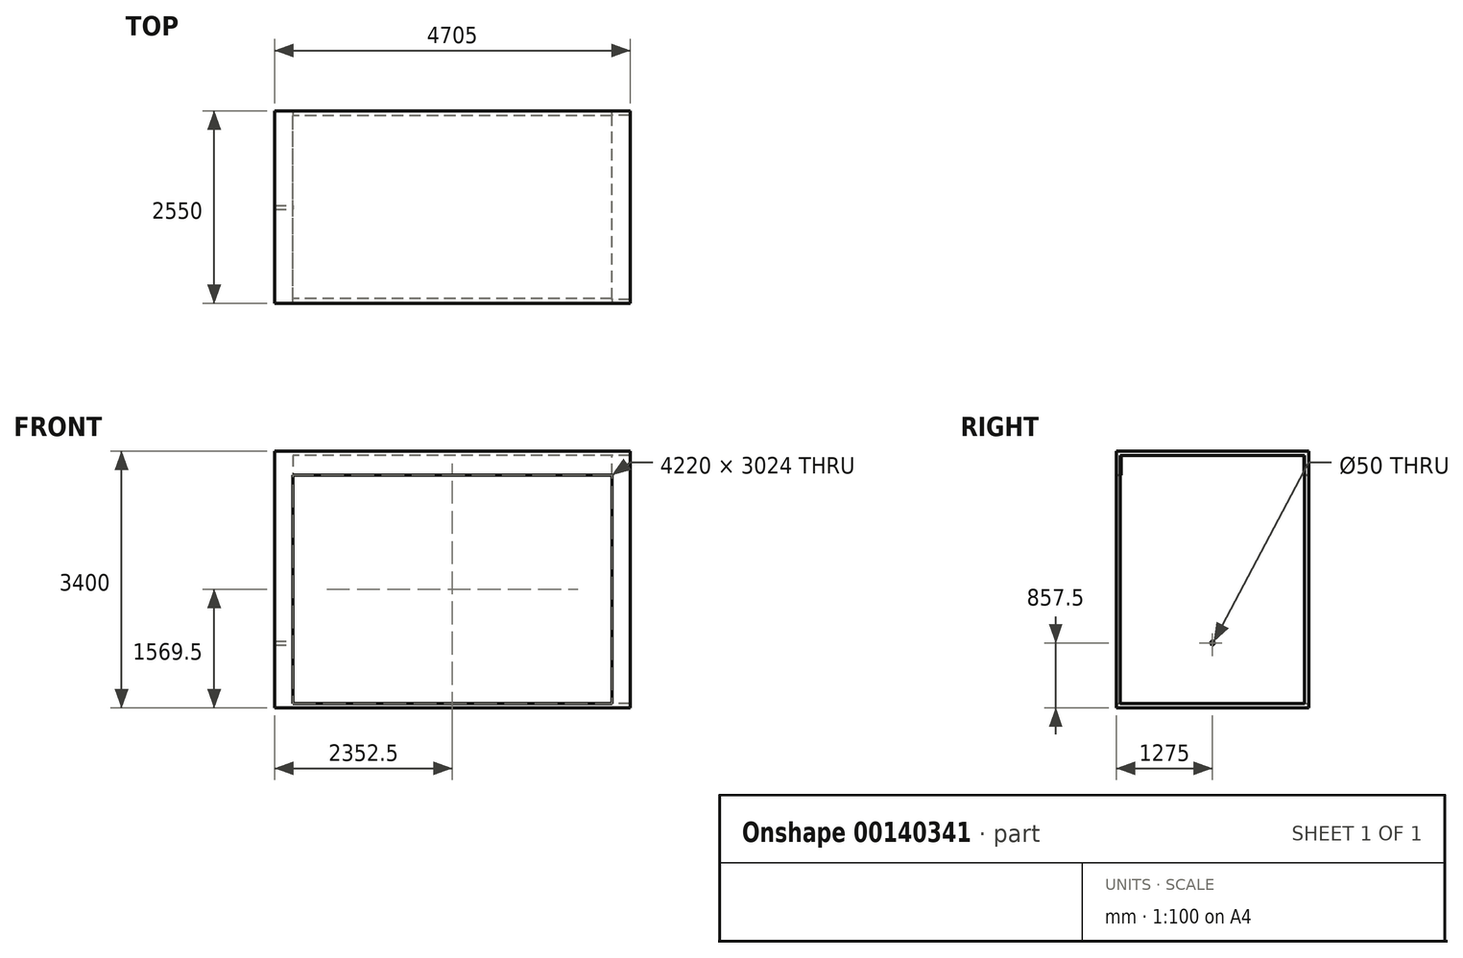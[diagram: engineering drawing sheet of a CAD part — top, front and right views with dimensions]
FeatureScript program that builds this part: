
annotation { "Feature Type Name" : "Feature", "Feature Type Description" : "" }
export const myFeature = defineFeature(function(context is Context, id is Id, definition is map)
    precondition{}
    {
        {
            var Q0;
            Q0=qCreatedBy(makeId("Front.planeOp"),FACE);
            var sketch = newSketch(context, id + "F0", { "sketchPlane" : qUnion([Q0])});
            skLineSegment(sketch, "E0.bottom", {"start": v(2352.5, -1700) * mm, "end": v(-2352.5, -1700) * mm});
            skLineSegment(sketch, "E0.top", {"start": v(2352.5, 1700) * mm, "end": v(-2352.5, 1700) * mm});
            skLineSegment(sketch, "E0.left", {"start": v(2352.5, -1700) * mm, "end": v(2352.5, 1700) * mm});
            skLineSegment(sketch, "E0.right", {"start": v(-2352.5, -1700) * mm, "end": v(-2352.5, 1700) * mm});
            skPoint(sketch, "E0.middle", {"position": v(0, 0) * mm});
            skLineSegment(sketch, "E1.bottom", {"start": v(2110, -1642.5) * mm, "end": v(-2110, -1642.5) * mm});
            skLineSegment(sketch, "E1.top", {"start": v(2110, 1642.5) * mm, "end": v(-2110, 1642.5) * mm});
            skLineSegment(sketch, "E1.left", {"start": v(2110, -1642.5) * mm, "end": v(2110, 1642.5) * mm});
            skLineSegment(sketch, "E1.right", {"start": v(-2110, -1642.5) * mm, "end": v(-2110, 1642.5) * mm});
            skSolve(sketch);
        }
        {
            var Q0;
            Q0=qSketchRegion(id+"F0",true);
            extrude(context, id + "F1", {"entities" : qUnion([Q0]), "depth" : 2550 * mm});
        }
        {
            var Q0;
            Q0=makeQuery(id+"F1.opExtrude","SWEPT_FACE",FACE,{"disambiguationData":[OSD([sQuery(id+"F0.wireOp",EDGE,"E1.right")])]});
            var sketch = newSketch(context, id + "F2", { "sketchPlane" : qUnion([Q0])});
            skLineSegment(sketch, "E2.bottom", {"start": v(-2550, 1642.5) * mm, "end": v(-2485, 1642.5) * mm});
            skLineSegment(sketch, "E2.top", {"start": v(-2550, 1381.5) * mm, "end": v(-2485, 1381.5) * mm});
            skLineSegment(sketch, "E2.left", {"start": v(-2550, 1642.5) * mm, "end": v(-2550, 1381.5) * mm});
            skLineSegment(sketch, "E2.right", {"start": v(-2485, 1642.5) * mm, "end": v(-2485, 1381.5) * mm});
            skLineSegment(sketch, "E3", {"start": v(-1275, -1642.5) * mm, "end": v(-1275, 507.53) * mm, "construction": true});
            skLineSegment(sketch, "E4.MirrorCS", {"start": v(0, 1642.5) * mm, "end": v(0, 1381.5) * mm});
            skLineSegment(sketch, "E5.MirrorCS", {"start": v(-65, 1642.5) * mm, "end": v(-65, 1381.5) * mm});
            skLineSegment(sketch, "E6.MirrorCS", {"start": v(0, 1381.5) * mm, "end": v(-65, 1381.5) * mm});
            skLineSegment(sketch, "E7.MirrorCS", {"start": v(0, 1642.5) * mm, "end": v(-65, 1642.5) * mm});
            skSolve(sketch);
        }
        {
            var Q0;
            Q0 = qSketchRegion(id + "F2", true);
            extrude(context, id + "F3", {"entities" : qUnion([Q0]), "operationType" : NewBodyOperationType.ADD, "endBound" : BoundingType.UP_TO_NEXT, "depth" : 25 * mm});
        }
        {
            var Q0;
            Q0=makeQuery(id+"F1.opExtrude","SWEPT_FACE",FACE,{"disambiguationData":[OSD([sQuery(id+"F0.wireOp",EDGE,"E1.left")])]});
            var sketch = newSketch(context, id + "F4", { "sketchPlane" : qUnion([Q0])});
            skLineSegment(sketch, "E8", {"start": v(1275, -1642.5) * mm, "end": v(1275, 656.22) * mm, "construction": true});
            skLineSegment(sketch, "E9.bottom", {"start": v(55, 1642.5) * mm, "end": v(2495, 1642.5) * mm});
            skLineSegment(sketch, "E9.top", {"start": v(55, -1642.5) * mm, "end": v(2495, -1642.5) * mm});
            skLineSegment(sketch, "E9.left", {"start": v(55, 1642.5) * mm, "end": v(55, -1642.5) * mm});
            skLineSegment(sketch, "E9.right", {"start": v(2495, 1642.5) * mm, "end": v(2495, -1642.5) * mm});
            skPoint(sketch, "E9.middle", {"position": v(1275, 0) * mm});
            skSolve(sketch);
        }
        {
            var Q0;
            Q0 = qSketchRegion(id + "F4", true);
            extrude(context, id + "F5", {"entities" : qUnion([Q0]), "operationType" : NewBodyOperationType.REMOVE, "endBound" : BoundingType.UP_TO_NEXT, "oppositeDirection" : true, "depth" : 25 * mm});
        }
        {
            var Q0;
            Q0=makeQuery(id+"F1.opExtrude","SWEPT_FACE",FACE,{"disambiguationData":[OSD([sQuery(id+"F0.wireOp",EDGE,"E1.right")])]});
            var sketch = newSketch(context, id + "F6", { "sketchPlane" : qUnion([Q0])});
            skLineSegment(sketch, "E10", {"start": v(-1275, -1642.5) * mm, "end": v(-1275, 1642.5) * mm, "construction": true});
            skCircle(sketch, "E11", {"center": v(-1275, -842.5) * mm, "radius": 25 * mm});
            skSolve(sketch);
        }
        {
            var Q0;
            Q0 = qSketchRegion(id + "F6", true);
            extrude(context, id + "F7", {"entities" : qUnion([Q0]), "operationType" : NewBodyOperationType.REMOVE, "endBound" : BoundingType.THROUGH_ALL, "oppositeDirection" : true, "depth" : 25 * mm});
        }
        {
            var Q0;
            Q0=makeQuery(id+"F3.boolean.opBoolean","MERGE",FACE,{"derivedFrom":[makeQuery(id+"F1.opExtrude","CAP_FACE",FACE,{"disambiguationData":[OSD([sQuery(id+"F0.wireOp",EDGE,"E0.bottom"),sQuery(id+"F0.wireOp",EDGE,"E0.top"),sQuery(id+"F0.wireOp",EDGE,"E0.left"),sQuery(id+"F0.wireOp",EDGE,"E0.right"),sQuery(id+"F0.wireOp",EDGE,"E1.bottom"),sQuery(id+"F0.wireOp",EDGE,"E1.top"),sQuery(id+"F0.wireOp",EDGE,"E1.left"),sQuery(id+"F0.wireOp",EDGE,"E1.right")])],"isStart":true}),makeQuery(id+"F3.opExtrude","SWEPT_FACE",FACE,{"disambiguationData":[OSD([sQuery(id+"F2.wireOp",EDGE,"E4.MirrorCS")])]})]});
            var sketch = newSketch(context, id + "F8", { "sketchPlane" : qUnion([Q0])});
            skLineSegment(sketch, "E12", {"start": v(0, 1700) * mm, "end": v(0, 1526.46) * mm, "construction": true});
            skPoint(sketch, "E12.endSnap0", {"position": v(0, 1700) * mm});
            skLineSegment(sketch, "E13.bottom", {"start": v(-2110, 1700) * mm, "end": v(2110, 1700) * mm});
            skLineSegment(sketch, "E13.top", {"start": v(-2110, 1381.5) * mm, "end": v(2110, 1381.5) * mm});
            skLineSegment(sketch, "E13.left", {"start": v(-2110, 1700) * mm, "end": v(-2110, 1381.5) * mm});
            skLineSegment(sketch, "E13.right", {"start": v(2110, 1700) * mm, "end": v(2110, 1381.5) * mm});
            skPoint(sketch, "E13.middle", {"position": v(0, 1540.75) * mm});
            skSolve(sketch);
        }
        {
            var Q0;
            Q0=makeQuery(id+"F5.boolean.opBoolean","MERGE",FACE,{"derivedFrom":[makeQuery(id+"F1.opExtrude","SWEPT_FACE",FACE,{"disambiguationData":[OSD([sQuery(id+"F0.wireOp",EDGE,"E1.bottom")])]}),makeQuery(id+"F5.opExtrude","SWEPT_FACE",FACE,{"disambiguationData":[OSD([sQuery(id+"F4.wireOp",EDGE,"E9.top")])]})]});
            var sketch = newSketch(context, id + "F9", { "sketchPlane" : qUnion([Q0])});
            skLineSegment(sketch, "E14.bottom", {"start": v(2110, -2495) * mm, "end": v(2352.5, -2495) * mm});
            skLineSegment(sketch, "E14.top", {"start": v(2110, -55) * mm, "end": v(2352.5, -55) * mm});
            skLineSegment(sketch, "E14.left", {"start": v(2110, -2495) * mm, "end": v(2110, -55) * mm});
            skLineSegment(sketch, "E14.right", {"start": v(2352.5, -2495) * mm, "end": v(2352.5, -55) * mm});
            skSolve(sketch);
        }
        {
            var Q0;
            Q0 = qSketchRegion(id + "F9", true);
            extrude(context, id + "F10", {"entities" : qUnion([Q0]), "operationType" : NewBodyOperationType.REMOVE, "oppositeDirection" : true, "depth" : 1 * mm});
        }
    });
